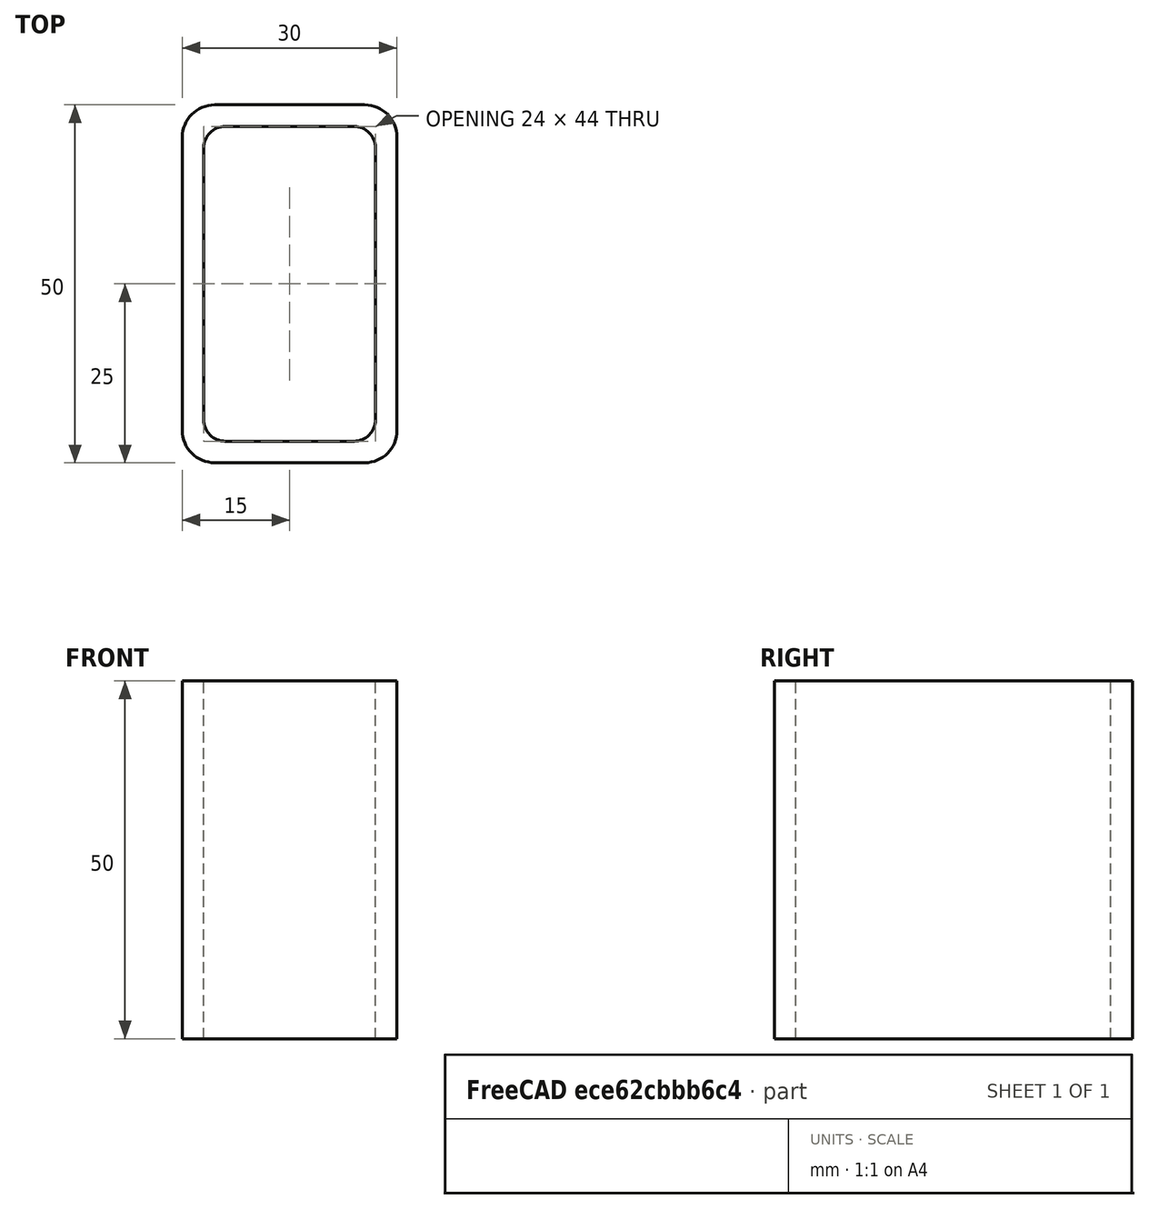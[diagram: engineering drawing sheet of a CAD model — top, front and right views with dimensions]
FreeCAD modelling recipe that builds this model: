
FCSTD DOCUMENT  (FreeCAD 0.15R4671 (Git))
Label: Rectangular hollow section 50x30x3 EN10219 S235JRH
License: All rights reserved
LicenseURL: http://en.wikipedia.org/wiki/All_rights_reserved
objects: Sketcher::SketchObject×1, Part::Extrusion×1
note: 2 computed .brp shape members not serialized (recipe doc carries the construction recipe); baked Part::Feature solids carry a one-line shape summary decoded from their .brp

FEATURE [Sketcher::SketchObject] Sketch
  sketch-geometry (16):
    g0: LineSegment StartX=-9 StartY=22 StartZ=0 EndX=9 EndY=22 EndZ=0
    g1: LineSegment StartX=12 StartY=19 StartZ=0 EndX=12 EndY=-19 EndZ=0
    g2: LineSegment StartX=9 StartY=-22 StartZ=0 EndX=-9 EndY=-22 EndZ=0
    g3: LineSegment StartX=-12 StartY=-19 StartZ=0 EndX=-12 EndY=19 EndZ=0
    g4: LineSegment StartX=-10.5 StartY=25 StartZ=0 EndX=10.5 EndY=25 EndZ=0
    g5: LineSegment StartX=15 StartY=20.5 StartZ=0 EndX=15 EndY=-20.5 EndZ=0
    g6: LineSegment StartX=10.5 StartY=-25 StartZ=0 EndX=-10.5 EndY=-25 EndZ=0
    g7: LineSegment StartX=-15 StartY=-20.5 StartZ=0 EndX=-15 EndY=20.5 EndZ=0
    g8: ArcOfCircle CenterX=-9 CenterY=19 CenterZ=0 NormalX=0 NormalY=0 NormalZ=1 Radius=3 StartAngle=1.5708 EndAngle=3.14159
    g9: ArcOfCircle CenterX=9 CenterY=19 CenterZ=0 NormalX=0 NormalY=0 NormalZ=1 Radius=3 StartAngle=0 EndAngle=1.5708
    g10: ArcOfCircle CenterX=9 CenterY=-19 CenterZ=0 NormalX=0 NormalY=0 NormalZ=1 Radius=3 StartAngle=4.71239 EndAngle=6.28319
    g11: ArcOfCircle CenterX=-9 CenterY=-19 CenterZ=0 NormalX=0 NormalY=0 NormalZ=1 Radius=3 StartAngle=3.14159 EndAngle=4.71239
    g12: ArcOfCircle CenterX=10.5 CenterY=20.5 CenterZ=0 NormalX=0 NormalY=0 NormalZ=1 Radius=4.5 StartAngle=0 EndAngle=1.5708
    g13: ArcOfCircle CenterX=10.5 CenterY=-20.5 CenterZ=0 NormalX=0 NormalY=0 NormalZ=1 Radius=4.5 StartAngle=4.71239 EndAngle=6.28319
    g14: ArcOfCircle CenterX=-10.5 CenterY=-20.5 CenterZ=0 NormalX=0 NormalY=0 NormalZ=1 Radius=4.5 StartAngle=3.14159 EndAngle=4.71239
    g15: ArcOfCircle CenterX=-10.5 CenterY=20.5 CenterZ=0 NormalX=0 NormalY=0 NormalZ=1 Radius=4.5 StartAngle=1.5708 EndAngle=3.14159
  constraints (36):
    c: Horizontal(g2)
    c: Vertical(g3)
    c: Horizontal(g6)
    c: Vertical(g7)
    c: Tangent(g3,g8) = 1.5708
    c: Tangent(g0,g8) = 1.5708
    c: Tangent(g0,g9) = 1.5708
    c: Tangent(g1,g9) = 1.5708
    c: Tangent(g1,g10) = 1.5708
    c: Tangent(g2,g10) = 1.5708
    c: Tangent(g2,g11) = 1.5708
    c: Tangent(g3,g11) = 1.5708
    c: Tangent(g4,g12) = 1.5708
    c: Tangent(g5,g12) = 1.5708
    c: Tangent(g5,g13) = 1.5708
    c: Tangent(g6,g13) = 1.5708
    c: Tangent(g6,g14) = 1.5708
    c: Tangent(g7,g14) = 1.5708
    c: Tangent(g7,g15) = 1.5708
    c: Tangent(g4,g15) = 1.5708
    c: Equal(g9,g8)
    c: Equal(g9,g11)
    c: Equal(g9,g10)
    c: Equal(g12,g15)
    c: Equal(g12,g14)
    c: Equal(g12,g13)
    c: Symmetric(g4,g6,g-1)
    c: Symmetric(g7,g5,g-2)
    c: DistanceY(g4,g6) = -50
    c: DistanceX(g7,g5) = 30
    c: Symmetric(g3,g1,g-2)
    c: Symmetric(g0,g2,g-1)
    c: DistanceY(g0,g4) = 3
    c: DistanceX(g5,g1) = -3
    c: Radius(g9) = 3
    c: Radius(g12) = 4.5
FEATURE [Part::Extrusion] Extrude  label="Rectangular hollow section 50x30x3 EN10219 S235JRH"
  Base = -> Sketch
  Dir = (0,0,50)
  Solid = true
